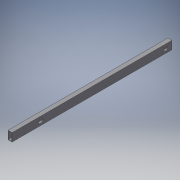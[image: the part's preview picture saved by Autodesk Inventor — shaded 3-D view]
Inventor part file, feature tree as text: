
AUTODESK INVENTOR PART (.ipt)
format: ipt  version: 2018 (Build 220112000, 112)  size: 165,376 bytes
history: native  units: in
note: dims shown in document units (in); Inventor stores cm internally (conversion verified against a paired STEP export)
features: extrude x6, sketch x6
ambient origin geometry x8: Origin, YZ Plane, XZ Plane, XY Plane, X Axis, Y Axis, Z Axis, Center Point
bodies: Solid1 (feature_tree)
feature tree (12):
  extrude  "Extrusion1"  Depth=2.0in
  extrude  "Extrusion2"  Depth=0.125in TaperAngle=0.0deg
  extrude  "Extrusion3"  Depth=0.5in TaperAngle=0.0deg
  extrude  "Extrusion7"  Depth=7.0in
  extrude  "Extrusion9"  Depth=1.0in TaperAngle=0.0deg
  extrude  "Extrusion10"  Depth=1.0in
  sketch  "Sketch1"  dims[d0=1.0in d1=2.0in]
  sketch  "Sketch2"  dims[d2=0.125in d3=38.5in d4=0.0in]
  sketch  "Sketch3"  dims[d5=1.0in d7=0.5in d8=0.0in]
  sketch  "Sketch7"  dims[d9=1.125in d10=7.0in]
  sketch  "Sketch9"  dims[d11=1.125in d12=1.0in d13=0.0in]
  sketch  "Sketch10"  dims[d34=1.0in d35=1.0in d36=0.5in d37=0.0in d44=0.9375in d45=0.2031in d46=0.2031in d47=0.2031in d48=0.2031in d49=1.0in d50=0.0in d51=0.125in d52=2.0in d53=1.0in d54=0.125in d55=0.125in d56=2.0in d57=1.0in d58=0.125in d59=0.5in d60=0.0in]
